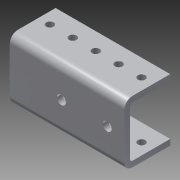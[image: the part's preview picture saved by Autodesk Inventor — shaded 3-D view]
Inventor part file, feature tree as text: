
AUTODESK INVENTOR PART (.ipt)
format: ipt  version: 2014 (Build 180170000, 170)  size: 142,336 bytes
history: native  units: in
note: dims shown in document units (in); Inventor stores cm internally (conversion verified against a paired STEP export)
features: sheet_metal_op x4, sketch x3, other x2, extrude x1
ambient origin geometry x8: Origin, YZ Plane, XZ Plane, XY Plane, X Axis, Y Axis, Z Axis, Center Point
bodies: Solid1 (feature_tree)
feature tree (10):
  sheet_metal_op  "Face1"
  sheet_metal_op  "Flange1"
  extrude  "Extrusion1"  Depth=1.0in
  sketch  "Sketch1"  dims[d0=2.5in d1=1.0in]
  other  "Plate1"
  sketch  "Sketch2"  dims[d2=0.196in]
  other  "Plate2"
  sheet_metal_op  "Bend1"
  sheet_metal_op  "Corner1"
  sketch  "Sketch3"  dims[d3=0.7874in d5=1.0in d6=0.3937in d8=1.0in d10=0.5in d11=1.125in d12=0.125in d13=0.125in d14=0.0625in d15=0.25in d16=0.125in d17=1.0in d18=90.0deg d19=0.05in d20=0.5in d21=0.125in d22=0.125in d23=0.163in d24=0.5in d25=0.25in d26=1.9685in d28=0.5in d29=0.3937in d31=1.0in d33=2.0in d34=0.0in]
